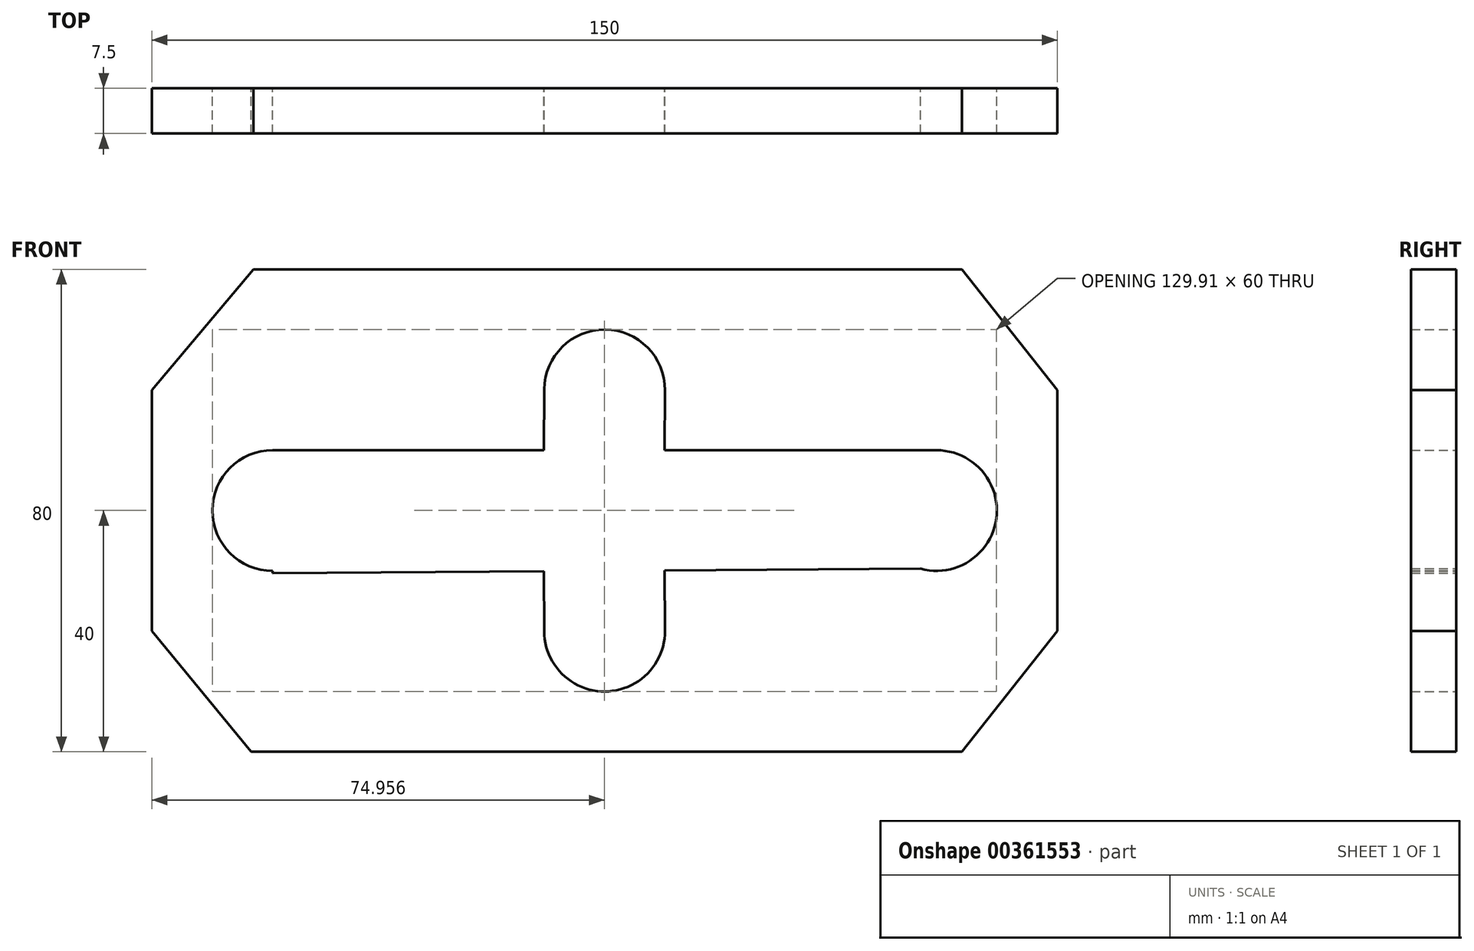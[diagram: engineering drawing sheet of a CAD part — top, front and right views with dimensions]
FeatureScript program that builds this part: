
annotation { "Feature Type Name" : "Feature", "Feature Type Description" : "" }
export const myFeature = defineFeature(function(context is Context, id is Id, definition is map)
    precondition{}
    {
        {
            var Q0;
            Q0=qCreatedBy(makeId("Front.planeOp"),FACE);
            var sketch = newSketch(context, id + "F0", { "sketchPlane" : qUnion([Q0])});
            skLineSegment(sketch, "E0", {"start": v(59.22, 40) * mm, "end": v(75, 20) * mm});
            skLineSegment(sketch, "E1", {"start": v(75, 20) * mm, "end": v(75, -20) * mm});
            skLineSegment(sketch, "E2", {"start": v(75, -20) * mm, "end": v(59.22, -40) * mm});
            skLineSegment(sketch, "E3", {"start": v(59.22, -40) * mm, "end": v(-58.58, -40) * mm});
            skLineSegment(sketch, "E4", {"start": v(-58.58, -40) * mm, "end": v(-75, -20) * mm});
            skLineSegment(sketch, "E5", {"start": v(-75, -20) * mm, "end": v(-75, 20) * mm});
            skLineSegment(sketch, "E6", {"start": v(-75, 20) * mm, "end": v(-58.22, 40) * mm});
            skLineSegment(sketch, "E7", {"start": v(-58.22, 40) * mm, "end": v(59.22, 40) * mm});
            skLineSegment(sketch, "E8", {"start": v(-55, -10.37) * mm, "end": v(-55, -10) * mm});
            skLineSegment(sketch, "E9", {"start": v(-55, 10) * mm, "end": v(-10.07, 10) * mm});
            skLineSegment(sketch, "E10", {"start": v(-55, -10.37) * mm, "end": v(-10.07, -10.07) * mm});
            skArc(sketch, "E11", {"start": v(-55, 10) * mm, "mid": v(-65, 0) * mm, "end": v(-55, -10) * mm});
            skArc(sketch, "E12", {"start": v(52.37, -9.65) * mm, "mid": v(64.91, -1.32) * mm, "end": v(55, 10) * mm});
            skArc(sketch, "E13", {"start": v(10, 19.93) * mm, "mid": v(0.07, 30) * mm, "end": v(-10, 20.07) * mm});
            skArc(sketch, "E14", {"start": v(-10, -20) * mm, "mid": v(0.03, -30) * mm, "end": v(10, -19.93) * mm});
            skLineSegment(sketch, "E15", {"start": v(0, -20) * mm, "end": v(10, -19.93) * mm});
            skLineSegment(sketch, "E16", {"start": v(10, -19.93) * mm, "end": v(9.93, -9.93) * mm});
            skLineSegment(sketch, "E17", {"start": v(0, -20) * mm, "end": v(-10, -20) * mm});
            skLineSegment(sketch, "E18", {"start": v(-10, -20) * mm, "end": v(-10.07, -10.07) * mm});
            skLineSegment(sketch, "E19", {"start": v(-10.07, 10) * mm, "end": v(-10, 20.07) * mm});
            skLineSegment(sketch, "E20", {"start": v(10, 19.93) * mm, "end": v(9.95, 10) * mm});
            skLineSegment(sketch, "E21.trimOffspring", {"start": v(9.95, 10) * mm, "end": v(55, 10) * mm});
            skLineSegment(sketch, "E22.trimOffspring", {"start": v(-0.16, -10) * mm, "end": v(0.03, -10) * mm});
            skLineSegment(sketch, "E23.trimOffspring", {"start": v(9.93, -9.93) * mm, "end": v(55, -9.63) * mm});
            skArc(sketch, "E24.trimOffspring", {"start": v(0.03, -10) * mm, "mid": v(-0.07, -10) * mm, "end": v(-0.16, -10) * mm});
            skPoint(sketch, "E25.orphan", {"position": v(9.87, 0) * mm});
            skPoint(sketch, "E26.orphan", {"position": v(-10.13, 0) * mm});
            skSolve(sketch);
        }
        {
            var Q0;
            Q0 = qSketchRegion(id + "F0", true);
            extrude(context, id + "F1", {"entities" : qUnion([Q0]), "depth" : 7.5 * mm});
        }
    });
